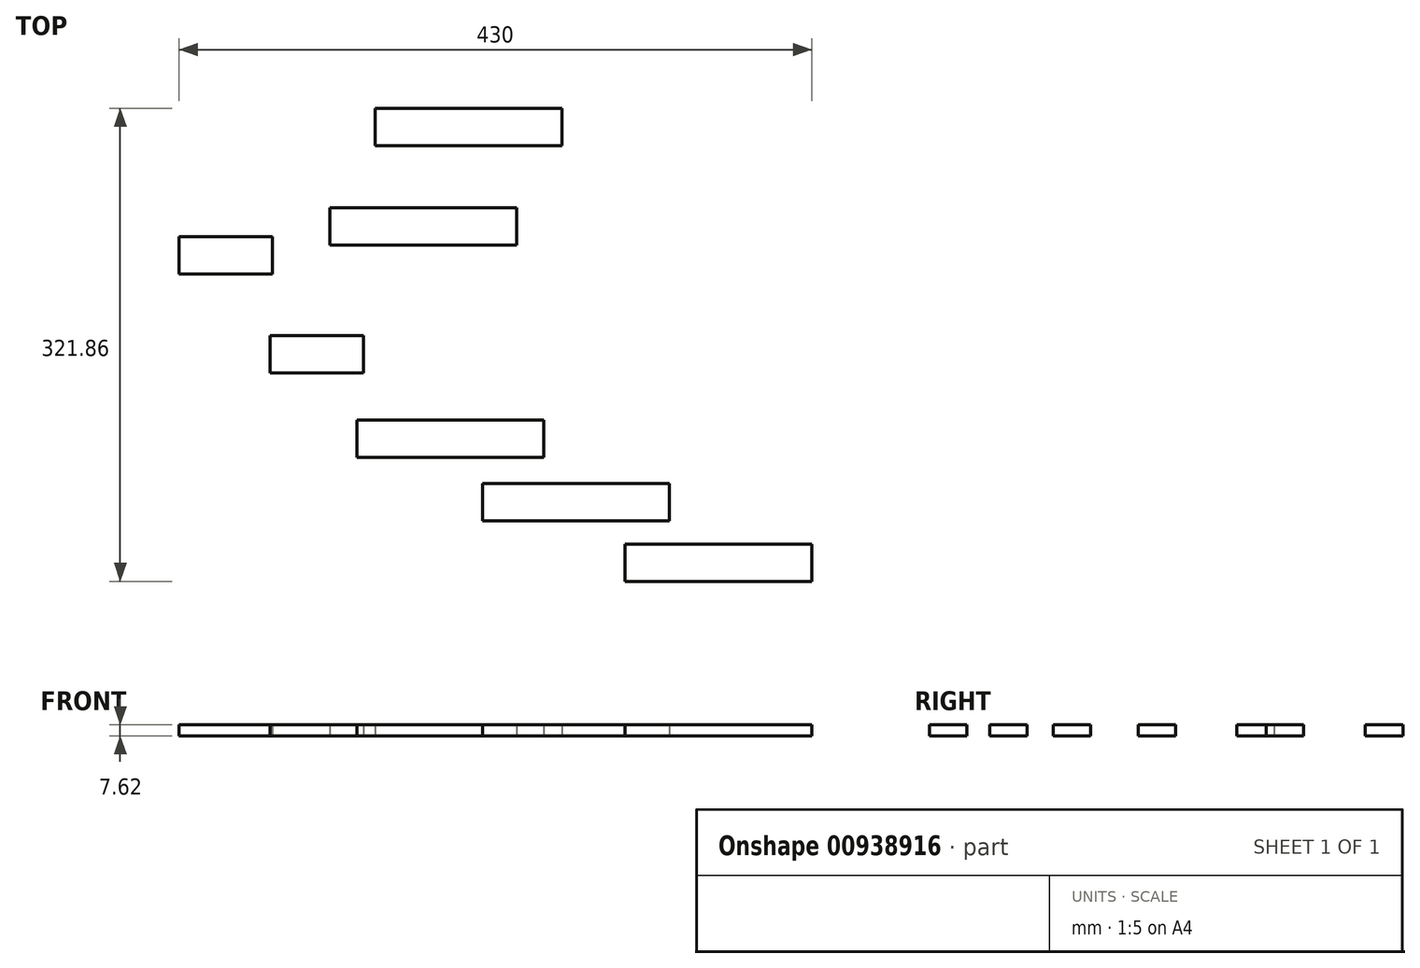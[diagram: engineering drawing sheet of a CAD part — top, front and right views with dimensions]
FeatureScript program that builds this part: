
annotation { "Feature Type Name" : "Feature", "Feature Type Description" : "" }
export const myFeature = defineFeature(function(context is Context, id is Id, definition is map)
    precondition{}
    {
        {
            var Q0;
            Q0=qCreatedBy(makeId("Top.planeOp"),FACE);
            var sketch = newSketch(context, id + "F0", { "sketchPlane" : qUnion([Q0])});
            skLineSegment(sketch, "E0.bottom", {"start": v(-214.98, -132.3) * mm, "end": v(-87.98, -132.3) * mm});
            skLineSegment(sketch, "E0.top", {"start": v(-214.98, -157.7) * mm, "end": v(-87.98, -157.7) * mm});
            skLineSegment(sketch, "E0.left", {"start": v(-214.98, -132.3) * mm, "end": v(-214.98, -157.7) * mm});
            skLineSegment(sketch, "E0.right", {"start": v(-87.98, -132.3) * mm, "end": v(-87.98, -157.7) * mm});
            skSolve(sketch);
        }
        {
            var Q0;
            Q0=qCreatedBy(makeId("Top.planeOp"),FACE);
            var sketch = newSketch(context, id + "F1", { "sketchPlane" : qUnion([Q0])});
            skLineSegment(sketch, "E1.bottom", {"start": v(-129.45, -175.52) * mm, "end": v(-2.45, -175.52) * mm});
            skLineSegment(sketch, "E1.top", {"start": v(-129.45, -200.92) * mm, "end": v(-2.45, -200.92) * mm});
            skLineSegment(sketch, "E1.left", {"start": v(-129.45, -175.52) * mm, "end": v(-129.45, -200.92) * mm});
            skLineSegment(sketch, "E1.right", {"start": v(-2.45, -175.52) * mm, "end": v(-2.45, -200.92) * mm});
            skLineSegment(sketch, "E2.bottom", {"start": v(-32.81, -216.62) * mm, "end": v(94.19, -216.62) * mm});
            skLineSegment(sketch, "E2.top", {"start": v(-32.81, -242.02) * mm, "end": v(94.19, -242.02) * mm});
            skLineSegment(sketch, "E2.left", {"start": v(-32.81, -216.62) * mm, "end": v(-32.81, -242.02) * mm});
            skLineSegment(sketch, "E2.right", {"start": v(94.19, -216.62) * mm, "end": v(94.19, -242.02) * mm});
            skLineSegment(sketch, "E3.bottom", {"start": v(-31.75, 12.7) * mm, "end": v(31.75, 12.7) * mm});
            skLineSegment(sketch, "E3.top", {"start": v(-31.75, -12.7) * mm, "end": v(31.75, -12.7) * mm});
            skLineSegment(sketch, "E3.left", {"start": v(-31.75, 12.7) * mm, "end": v(-31.75, -12.7) * mm});
            skLineSegment(sketch, "E3.right", {"start": v(31.75, 12.7) * mm, "end": v(31.75, -12.7) * mm});
            skSolve(sketch);
        }
        {
            var Q0;
            Q0=makeQuery(id+"F0.imprint","IMPRINT",FACE,{"disambiguationData":[TD([[makeQuery(id+"F0.imprint","IMPRINT",EDGE,{"derivedFrom":sQuery(id+"F0.wireOp",EDGE,"E0.bottom")}),-1.0]])]});
            var Q1;
            Q1=makeQuery(id+"F1.imprint","IMPRINT",FACE,{"disambiguationData":[TD([[makeQuery(id+"F1.imprint","IMPRINT",EDGE,{"derivedFrom":sQuery(id+"F1.wireOp",EDGE,"E1.bottom")}),-1.0]])]});
            var Q2;
            Q2=makeQuery(id+"F1.imprint","IMPRINT",FACE,{"disambiguationData":[TD([[makeQuery(id+"F1.imprint","IMPRINT",EDGE,{"derivedFrom":sQuery(id+"F1.wireOp",EDGE,"E2.bottom")}),-1.0]])]});
            extrude(context, id + "F2", {"entities" : qUnion([Q0, Q1, Q2]), "depth" : 7.62 * mm, "offsetDistance" : 25.4 * mm});
        }
        {
            var Q0;
            Q0=qCreatedBy(makeId("Top.planeOp"),FACE);
            var sketch = newSketch(context, id + "F3", { "sketchPlane" : qUnion([Q0])});
            skLineSegment(sketch, "E4.bottom", {"start": v(-274.18, -74.72) * mm, "end": v(-210.68, -74.72) * mm});
            skLineSegment(sketch, "E4.top", {"start": v(-274.18, -100.12) * mm, "end": v(-210.68, -100.12) * mm});
            skLineSegment(sketch, "E4.left", {"start": v(-274.18, -74.72) * mm, "end": v(-274.18, -100.12) * mm});
            skLineSegment(sketch, "E4.right", {"start": v(-210.68, -74.72) * mm, "end": v(-210.68, -100.12) * mm});
            skSolve(sketch);
        }
        {
            var Q0;
            Q0=makeQuery(id+"F3.imprint","IMPRINT",FACE,{"disambiguationData":[TD([[makeQuery(id+"F3.imprint","IMPRINT",EDGE,{"derivedFrom":sQuery(id+"F3.wireOp",EDGE,"E4.bottom")}),-1.0]])]});
            extrude(context, id + "F4", {"entities" : qUnion([Q0]), "depth" : 7.62 * mm, "offsetDistance" : 25.4 * mm});
        }
        {
            var Q0;
            Q0=qCreatedBy(makeId("Top.planeOp"),FACE);
            var sketch = newSketch(context, id + "F5", { "sketchPlane" : qUnion([Q0])});
            skLineSegment(sketch, "E5.bottom", {"start": v(-202.61, 79.84) * mm, "end": v(-75.61, 79.84) * mm});
            skLineSegment(sketch, "E5.top", {"start": v(-202.61, 54.44) * mm, "end": v(-75.61, 54.44) * mm});
            skLineSegment(sketch, "E5.left", {"start": v(-202.61, 79.84) * mm, "end": v(-202.61, 54.44) * mm});
            skLineSegment(sketch, "E5.right", {"start": v(-75.61, 79.84) * mm, "end": v(-75.61, 54.44) * mm});
            skLineSegment(sketch, "E6.bottom", {"start": v(-106.37, 12.26) * mm, "end": v(-233.37, 12.26) * mm});
            skLineSegment(sketch, "E6.top", {"start": v(-106.37, -13.14) * mm, "end": v(-233.37, -13.14) * mm});
            skLineSegment(sketch, "E6.left", {"start": v(-106.37, 12.26) * mm, "end": v(-106.37, -13.14) * mm});
            skLineSegment(sketch, "E6.right", {"start": v(-233.37, 12.26) * mm, "end": v(-233.37, -13.14) * mm});
            skSolve(sketch);
        }
        {
            var Q0;
            Q0=makeQuery(id+"F5.imprint","IMPRINT",FACE,{"disambiguationData":[TD([[makeQuery(id+"F5.imprint","IMPRINT",EDGE,{"derivedFrom":sQuery(id+"F5.wireOp",EDGE,"E5.bottom")}),-1.0]])]});
            var Q1;
            Q1=makeQuery(id+"F5.imprint","IMPRINT",FACE,{"disambiguationData":[TD([[makeQuery(id+"F5.imprint","IMPRINT",EDGE,{"derivedFrom":sQuery(id+"F5.wireOp",EDGE,"E6.bottom")}),1.0]])]});
            extrude(context, id + "F6", {"entities" : qUnion([Q0, Q1]), "depth" : 7.62 * mm, "offsetDistance" : 25.4 * mm});
        }
        {
            var Q0;
            Q0=qCreatedBy(makeId("Top.planeOp"),FACE);
            var sketch = newSketch(context, id + "F7", { "sketchPlane" : qUnion([Q0])});
            skLineSegment(sketch, "E7.bottom", {"start": v(-335.8, -32.98) * mm, "end": v(-272.3, -32.98) * mm});
            skLineSegment(sketch, "E7.top", {"start": v(-335.8, -7.58) * mm, "end": v(-272.3, -7.58) * mm});
            skLineSegment(sketch, "E7.left", {"start": v(-335.8, -32.98) * mm, "end": v(-335.8, -7.58) * mm});
            skLineSegment(sketch, "E7.right", {"start": v(-272.3, -32.98) * mm, "end": v(-272.3, -7.58) * mm});
            skSolve(sketch);
        }
        {
            var Q0;
            Q0=makeQuery(id+"F7.imprint","IMPRINT",FACE,{"disambiguationData":[TD([[makeQuery(id+"F7.imprint","IMPRINT",EDGE,{"derivedFrom":sQuery(id+"F7.wireOp",EDGE,"E7.bottom")}),1.0]])]});
            extrude(context, id + "F8", {"entities" : qUnion([Q0]), "depth" : 7.62 * mm, "offsetDistance" : 25.4 * mm});
        }
    });
